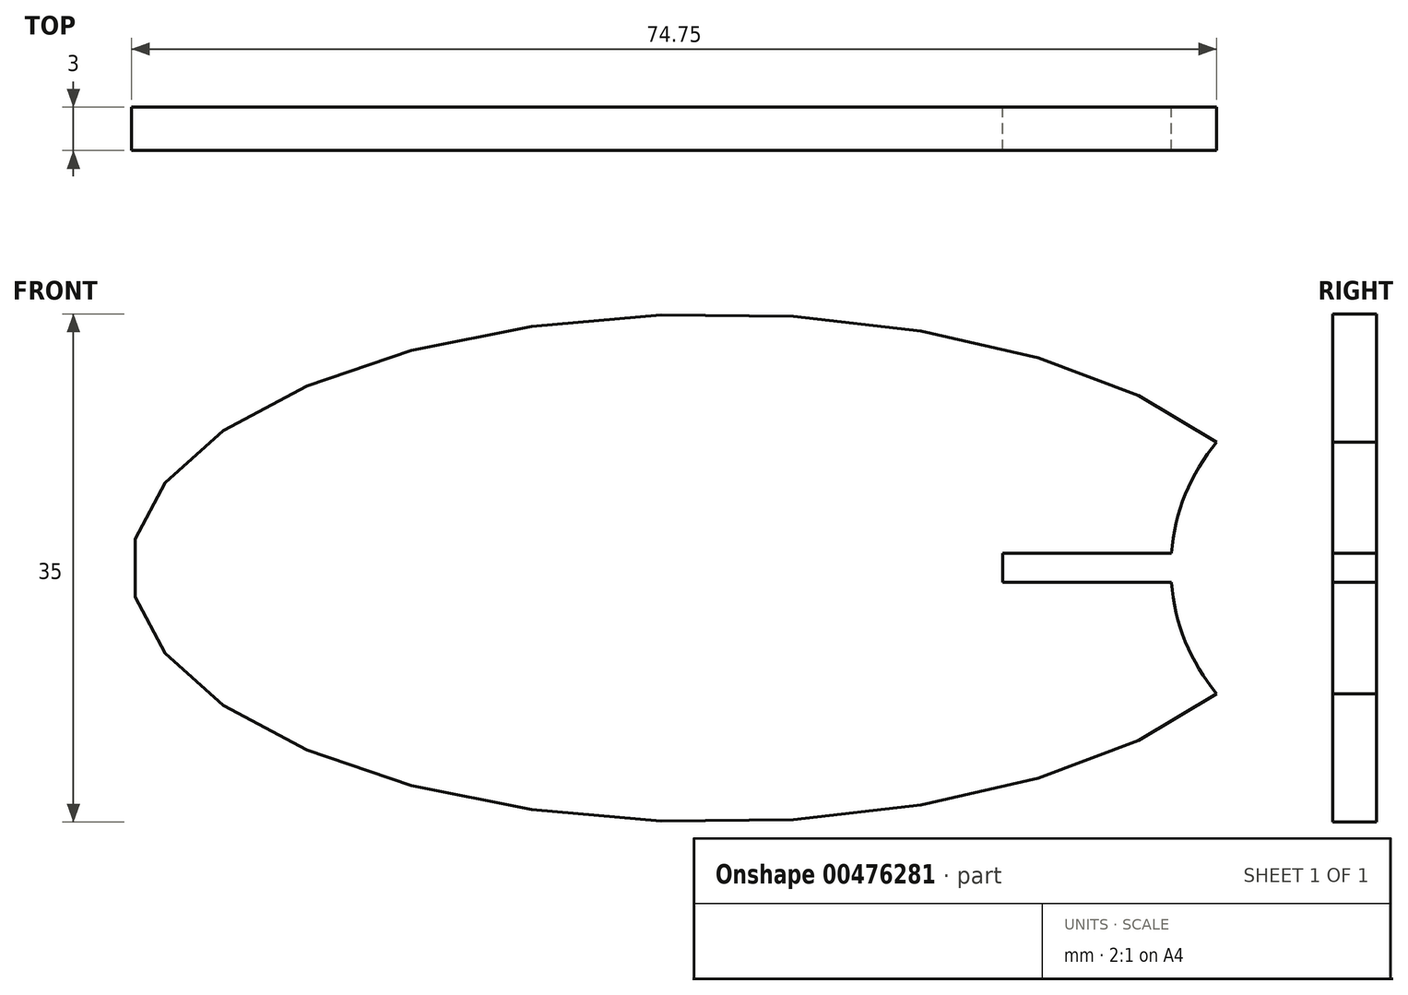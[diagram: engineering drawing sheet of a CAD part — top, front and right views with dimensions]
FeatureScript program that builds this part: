
annotation { "Feature Type Name" : "Feature", "Feature Type Description" : "" }
export const myFeature = defineFeature(function(context is Context, id is Id, definition is map)
    precondition{}
    {
        {
            var Q0;
            Q0=qCreatedBy(makeId("Front.planeOp"),FACE);
            var sketch = newSketch(context, id + "F0", { "sketchPlane" : qUnion([Q0])});
            skEllipse(sketch, "E0", {"center": v(0, 0) * mm, "majorRadius": 40 * mm, "minorRadius": 17.5 * mm, "majorAxis": v(-1, 0)});
            skSolve(sketch);
        }
        {
            var Q0;
            Q0 = qSketchRegion(id + "F0", true);
            extrude(context, id + "F1", {"entities" : qUnion([Q0]), "depth" : 3 * mm});
        }
        {
            var Q0;
            Q0=qCreatedBy(makeId("Front.planeOp"),FACE);
            var sketch = newSketch(context, id + "F2", { "sketchPlane" : qUnion([Q0])});
            skCircle(sketch, "E1", {"center": v(45.1, 0) * mm, "radius": 13.5 * mm});
            skSolve(sketch);
        }
        {
            var Q0;
            Q0 = qSketchRegion(id + "F2", true);
            extrude(context, id + "F3", {"entities" : qUnion([Q0]), "operationType" : NewBodyOperationType.REMOVE, "depth" : 25 * mm});
        }
        {
            var Q0;
            Q0=qCreatedBy(makeId("Front.planeOp"),FACE);
            var sketch = newSketch(context, id + "F4", { "sketchPlane" : qUnion([Q0])});
            skLineSegment(sketch, "E2.bottom", {"start": v(20, 1) * mm, "end": v(40, 1) * mm});
            skLineSegment(sketch, "E2.top", {"start": v(20, 0) * mm, "end": v(40, 0) * mm});
            skLineSegment(sketch, "E2.left", {"start": v(20, 1) * mm, "end": v(20, 0) * mm});
            skLineSegment(sketch, "E2.right", {"start": v(40, 1) * mm, "end": v(40, 0) * mm});
            skLineSegment(sketch, "E3.MirrorCS", {"start": v(20, -1) * mm, "end": v(40, -1) * mm});
            skLineSegment(sketch, "E4.MirrorCS", {"start": v(40, -1) * mm, "end": v(40, 0) * mm});
            skLineSegment(sketch, "E5.MirrorCS", {"start": v(20, -1) * mm, "end": v(20, 0) * mm});
            skSolve(sketch);
        }
        {
            var Q0;
            Q0 = qSketchRegion(id + "F4", true);
            extrude(context, id + "F5", {"entities" : qUnion([Q0]), "operationType" : NewBodyOperationType.REMOVE, "depth" : 25 * mm});
        }
    });
